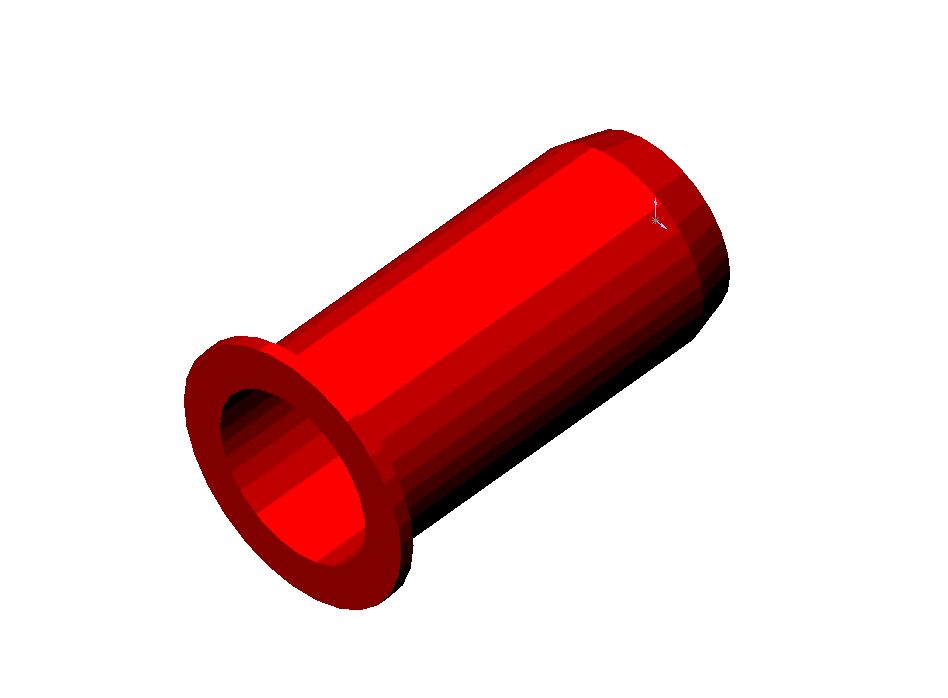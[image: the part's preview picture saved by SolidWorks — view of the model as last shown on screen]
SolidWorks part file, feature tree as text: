
SOLIDWORKS PART (.sldprt)
format: sldprt  version: not decoded by parser v0  size: 91,136 bytes
history: native  units: mm
features: plane x3, sketch x2, extrude x2, material x1, chamfer x1 (+10 scaffold rows collapsed)
feature tree (19):
  scaffold x10  (default folders/planes/origin — collapsed)
  material  "Matériau <non spécifié>"
  plane  "Plan1"
  plane  "Plan2"
  plane  "Plan3"
  sketch  "Esquisse1"  dims[D1=7.0mm D2=6.0mm]
  extrude  "Base-Extrusion"  Depth=14.5mm
  sketch  "Esquisse2"  dims[D1=9.0mm]
  extrude  "Boss.-Extru.1"  Depth=0.5mm
  chamfer  "Chanfrein1"  Distance=1.5mm Angle=15deg
decode coverage: 5 of 5 modeling features carry decoded parameters
note: suppression state not decoded; provenance and decode notes live in map.json
